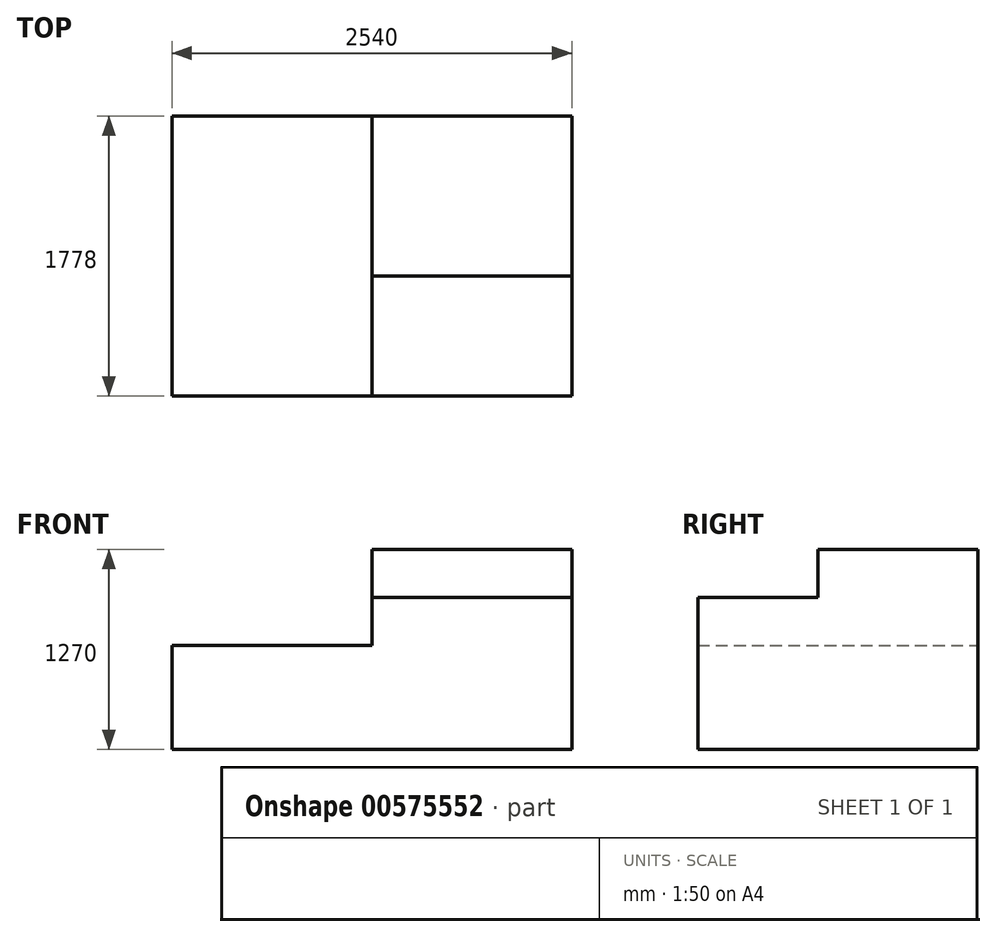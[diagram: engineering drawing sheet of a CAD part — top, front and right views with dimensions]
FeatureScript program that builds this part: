
annotation { "Feature Type Name" : "Feature", "Feature Type Description" : "" }
export const myFeature = defineFeature(function(context is Context, id is Id, definition is map)
    precondition{}
    {
        {
            var Q0;
            Q0=qCreatedBy(makeId("Front.planeOp"),FACE);
            var sketch = newSketch(context, id + "F0", { "sketchPlane" : qUnion([Q0])});
            skLineSegment(sketch, "E0", {"start": v(0, 0) * mm, "end": v(2540, 0) * mm});
            skLineSegment(sketch, "E1", {"start": v(2540, 0) * mm, "end": v(2540, 965.2) * mm});
            skLineSegment(sketch, "E2", {"start": v(0, 0) * mm, "end": v(0, 635) * mm});
            skLineSegment(sketch, "E3", {"start": v(2540, 965.2) * mm, "end": v(1270, 965.2) * mm});
            skLineSegment(sketch, "E4", {"start": v(1270, 965.2) * mm, "end": v(1270, 660.4) * mm});
            skLineSegment(sketch, "E5", {"start": v(1270, 660.4) * mm, "end": v(0, 660.4) * mm});
            skLineSegment(sketch, "E6", {"start": v(0, 660.4) * mm, "end": v(0, 635) * mm});
            skLineSegment(sketch, "E7", {"start": v(1270, 965.2) * mm, "end": v(1270, 1270) * mm});
            skLineSegment(sketch, "E8", {"start": v(1270, 1270) * mm, "end": v(2540, 1270) * mm});
            skLineSegment(sketch, "E9", {"start": v(2540, 1270) * mm, "end": v(2540, 965.2) * mm});
            skSolve(sketch);
        }
        {
            var Q0;
            Q0=makeQuery(id+"F0.imprint","IMPRINT",FACE,{"disambiguationData":[TD([[makeQuery(id+"F0.imprint","IMPRINT",EDGE,{"derivedFrom":sQuery(id+"F0.wireOp",EDGE,"E0")}),1.0]])]});
            extrude(context, id + "F1", {"entities" : qUnion([Q0]), "depth" : 1778 * mm, "offsetDistance" : 25.4 * mm});
        }
        {
            var Q0;
            Q0=makeQuery(id+"F0.imprint","IMPRINT",FACE,{"disambiguationData":[TD([[makeQuery(id+"F0.imprint","IMPRINT",EDGE,{"derivedFrom":sQuery(id+"F0.wireOp",EDGE,"E3")}),-1.0]])]});
            extrude(context, id + "F2", {"entities" : qUnion([Q0]), "operationType" : NewBodyOperationType.ADD, "depth" : 1016 * mm, "offsetDistance" : 25.4 * mm});
        }
    });
